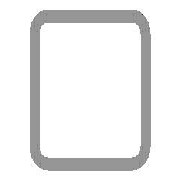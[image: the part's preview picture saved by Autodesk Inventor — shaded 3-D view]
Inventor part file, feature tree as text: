
AUTODESK INVENTOR PART (.ipt)
format: ipt  version: 2025 (Build 290162010, 162A)  size: 147,968 bytes
history: native  units: mm (DEFAULTED — no unit token found)
features: other x3, sketch x2, projected_geometry x2, extrude x1, plane x1
ambient origin geometry x8: Origin, YZ Plane, XZ Plane, XY Plane, X Axis, Y Axis, Z Axis, Center Point
bodies: Solid1 (feature_tree), Body (feature_tree)
feature tree (9):
  other  "Driven Length"
  other  "Start plane"
  other  "End plane"
  extrude  "Extrusion2"  TaperAngle=0.0deg  [1 undecoded]
  sketch  "Sketch3"  dims[d3=500.0mm d4=0.0mm]
  plane  "Work Plane3"
  sketch  "Sketch5"  dims[d7=4.0mm d9=40.0mm d11=40.0mm d12=2.0mm d13=-0.0mm d14=500.0mm d15=20.0mm d16=20.0mm d17=90.0deg d18=500.0mm d20=5.759587mm d21=0.0mm d22=0.0mm]
  projected_geometry  "Projected Loop1"
  projected_geometry  "Projected Loop2"
note: 1 required parameter value undecoded (feature->parameter linkage not recoverable at this tier; creation-order binding heuristic only, values carry confidence <= 0.55)
